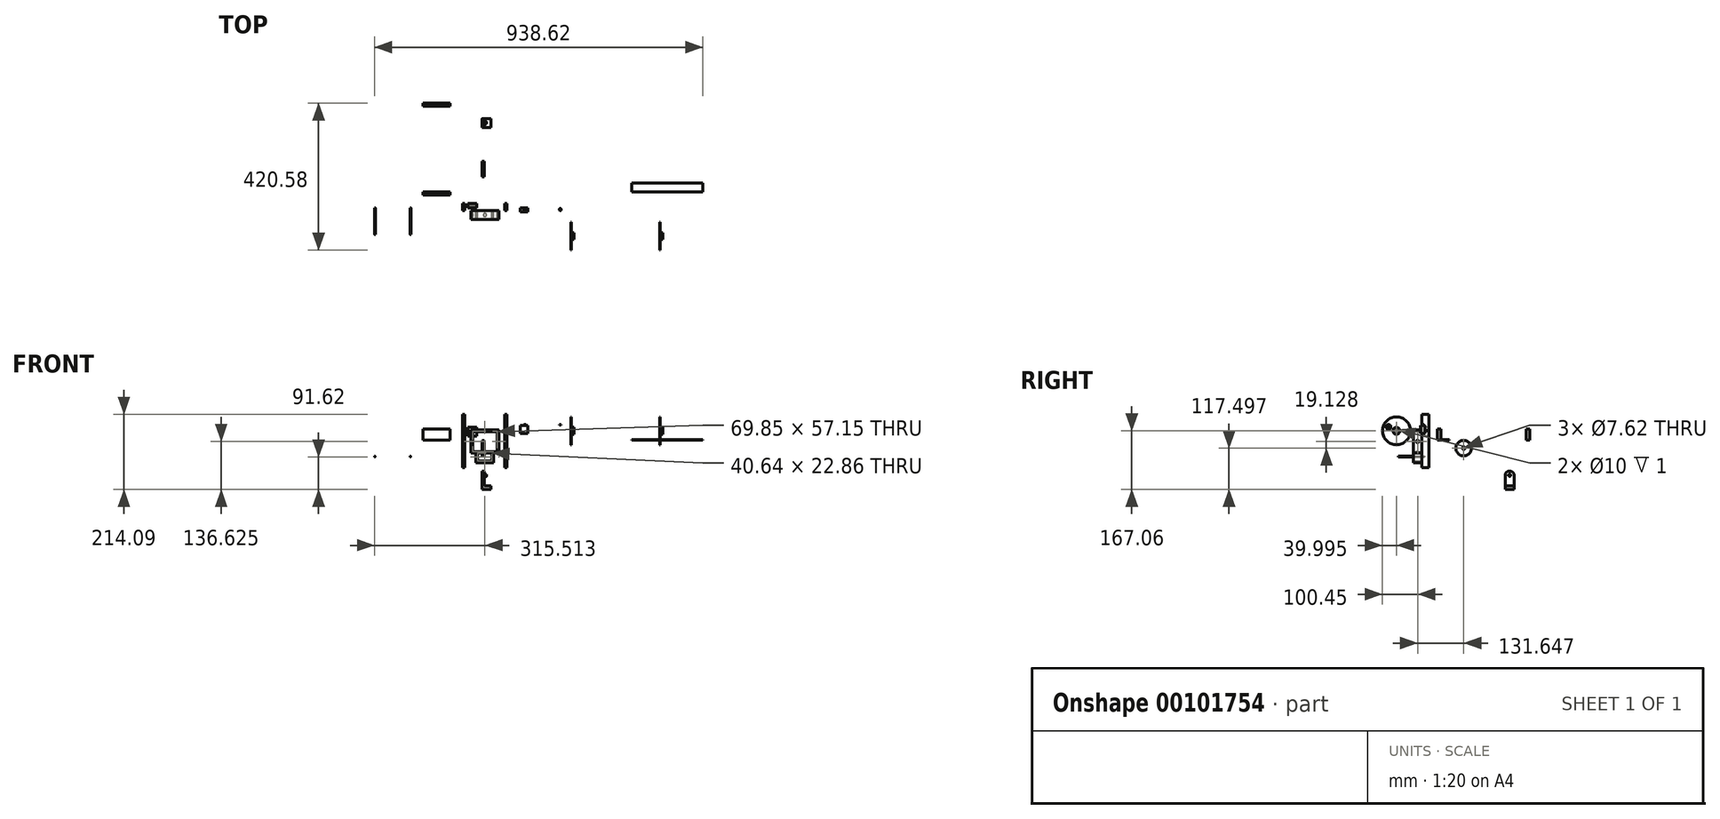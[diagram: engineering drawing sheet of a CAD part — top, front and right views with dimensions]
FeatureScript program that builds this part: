
annotation { "Feature Type Name" : "Feature", "Feature Type Description" : "" }
export const myFeature = defineFeature(function(context is Context, id is Id, definition is map)
    precondition{}
    {
        {
            var Q0;
            Q0=qCreatedBy(makeId("Front.planeOp"),FACE);
            var sketch = newSketch(context, id + "F0", { "sketchPlane" : qUnion([Q0])});
            skLineSegment(sketch, "E0.bottom", {"start": v(-56.2, 74.1) * mm, "end": v(70.8, 74.1) * mm});
            skLineSegment(sketch, "E0.top", {"start": v(-56.2, -78.3) * mm, "end": v(70.8, -78.3) * mm});
            skLineSegment(sketch, "E0.left", {"start": v(-56.2, 74.1) * mm, "end": v(-56.2, -78.3) * mm});
            skLineSegment(sketch, "E0.right", {"start": v(70.8, 74.1) * mm, "end": v(70.8, -78.3) * mm});
            skLineSegment(sketch, "E1", {"start": v(64.45, 74.1) * mm, "end": v(64.45, -78.3) * mm});
            skLineSegment(sketch, "E2", {"start": v(-49.85, 74.1) * mm, "end": v(-49.85, -78.3) * mm});
            skLineSegment(sketch, "E3", {"start": v(70.8, 74.1) * mm, "end": v(64.45, 74.1) * mm});
            skLineSegment(sketch, "E4", {"start": v(70.8, -78.3) * mm, "end": v(64.45, -78.3) * mm});
            skLineSegment(sketch, "E5", {"start": v(-49.85, 74.1) * mm, "end": v(-56.2, 74.1) * mm});
            skLineSegment(sketch, "E6", {"start": v(-49.85, -78.3) * mm, "end": v(-56.2, -78.3) * mm});
            skLineSegment(sketch, "E7", {"start": v(70.8, 10.6) * mm, "end": v(70.8, -11.63) * mm});
            skLineSegment(sketch, "E8", {"start": v(-49.85, 10.6) * mm, "end": v(-49.85, -11.63) * mm});
            skLineSegment(sketch, "E9", {"start": v(70.8, 10.6) * mm, "end": v(70.8, 74.1) * mm});
            skLineSegment(sketch, "E10", {"start": v(-49.85, 10.6) * mm, "end": v(-49.85, 74.1) * mm});
            skLineSegment(sketch, "E11", {"start": v(-49.85, 10.6) * mm, "end": v(-56.2, 10.6) * mm});
            skLineSegment(sketch, "E12", {"start": v(-49.85, -11.63) * mm, "end": v(-56.2, -11.63) * mm});
            skLineSegment(sketch, "E13", {"start": v(70.8, 10.6) * mm, "end": v(64.45, 10.6) * mm});
            skLineSegment(sketch, "E14", {"start": v(70.8, -11.63) * mm, "end": v(64.45, -11.63) * mm});
            skLineSegment(sketch, "E15", {"start": v(64.45, 10.6) * mm, "end": v(64.45, -11.63) * mm});
            skLineSegment(sketch, "E16", {"start": v(-56.2, 10.6) * mm, "end": v(-56.2, -11.63) * mm});
            skSolve(sketch);
        }
        {
            var Q0;
            Q0=makeQuery(id+"F0.imprint","IMPRINT",FACE,{"disambiguationData":[TD([[makeQuery(id+"F0.imprint","IMPRINT",EDGE,{"derivedFrom":sQuery(id+"F0.wireOp",EDGE,"E0.left")}),1.0]])]});
            var Q1;
            Q1=makeQuery(id+"F0.imprint","IMPRINT",FACE,{"disambiguationData":[TD([[makeQuery(id+"F0.imprint","IMPRINT",EDGE,{"derivedFrom":sQuery(id+"F0.wireOp",EDGE,"E0.right")}),-1.0]])]});
            var Q2;
            {var subQ0=sQuery(id+"F0.wireOp",EDGE,"E3");Q2=makeQuery(id+"F0.imprint","IMPRINT",FACE,{"disambiguationData":[TD([[makeQuery(id+"F0.imprint","IMPRINT",EDGE,{"derivedFrom":subQ0}),1.0]])]});}
            var Q3;
            {var subQ3=sQuery(id+"F0.wireOp",EDGE,"E0.bottom");Q3=makeQuery(id+"F0.imprint","IMPRINT",FACE,{"disambiguationData":[TD([[makeQuery(id+"F0.imprint","IMPRINT",EDGE,{"derivedFrom":subQ3}),-1.0]])]});}
            var Q4;
            Q4=makeQuery(id+"F0.imprint","IMPRINT",FACE,{"disambiguationData":[TD([[makeQuery(id+"F0.imprint","IMPRINT",EDGE,{"derivedFrom":sQuery(id+"F0.wireOp",EDGE,"E8")}),-1.0]])]});
            var Q5;
            Q5=makeQuery(id+"F0.imprint","IMPRINT",FACE,{"disambiguationData":[TD([[makeQuery(id+"F0.imprint","IMPRINT",EDGE,{"derivedFrom":sQuery(id+"F0.wireOp",EDGE,"E7")}),-1.0]])]});
            extrude(context, id + "F1", {"entities" : qUnion([Q0, Q1, Q2, Q3, Q4, Q5]), "depth" : 7.62 * mm});
        }
        {
            var Q0;
            Q0=qCreatedBy(makeId("Front.planeOp"),FACE);
            var sketch = newSketch(context, id + "F2", { "sketchPlane" : qUnion([Q0])});
            skLineSegment(sketch, "E17.bottom", {"start": v(108.57, 41.83) * mm, "end": v(130.8, 41.83) * mm});
            skLineSegment(sketch, "E17.top", {"start": v(108.57, 19.6) * mm, "end": v(130.8, 19.6) * mm});
            skLineSegment(sketch, "E17.left", {"start": v(108.57, 41.83) * mm, "end": v(108.57, 19.6) * mm});
            skLineSegment(sketch, "E17.right", {"start": v(130.8, 41.83) * mm, "end": v(130.8, 19.6) * mm});
            skSolve(sketch);
        }
        {
            var Q0;
            Q0=makeQuery(id+"F2.imprint","IMPRINT",FACE,{"disambiguationData":[TD([[makeQuery(id+"F2.imprint","IMPRINT",EDGE,{"derivedFrom":sQuery(id+"F2.wireOp",EDGE,"E17.bottom")}),-1.0]])]});
            extrude(context, id + "F3", {"entities" : qUnion([Q0]), "depth" : 11.94 * mm});
        }
        {
            var Q0;
            Q0=makeQuery(id+"F3.opExtrude","SWEPT_BODY",BODY,{"disambiguationData":[OSD([sQuery(id+"F2.wireOp",EDGE,"E17.bottom"),sQuery(id+"F2.wireOp",EDGE,"E17.top"),sQuery(id+"F2.wireOp",EDGE,"E17.left"),sQuery(id+"F2.wireOp",EDGE,"E17.right")])]});
            transform(context, id + "F4", {"entities" : qUnion([Q0]), "transformType" : TransformType.TRANSLATION_3D, "dx" : 76.2 * mm, "dy" : 0 * mm, "dz" : 0 * mm, "makeCopy" : true});
        }
        {
            var Q0;
            Q0=makeQuery(id+"F1.opExtrude","CAP_FACE",FACE,{"disambiguationData":[OSD([sQuery(id+"F0.wireOp",EDGE,"E0.bottom"),sQuery(id+"F0.wireOp",EDGE,"E0.top"),sQuery(id+"F0.wireOp",EDGE,"E0.left"),sQuery(id+"F0.wireOp",EDGE,"E0.right")])],"isStart":false});
            var sketch = newSketch(context, id + "F5", { "sketchPlane" : qUnion([Q0])});
            skLineSegment(sketch, "E18.bottom", {"start": v(-27, 25.2) * mm, "end": v(42.85, 25.2) * mm});
            skLineSegment(sketch, "E18.top", {"start": v(-27, -31.95) * mm, "end": v(42.85, -31.95) * mm});
            skLineSegment(sketch, "E18.left", {"start": v(-27, 25.2) * mm, "end": v(-27, -31.95) * mm});
            skLineSegment(sketch, "E18.right", {"start": v(42.85, 25.2) * mm, "end": v(42.85, -31.95) * mm});
            skLineSegment(sketch, "E19.bottom", {"start": v(-32, 30.2) * mm, "end": v(47.85, 30.2) * mm});
            skLineSegment(sketch, "E19.left", {"start": v(-32, 30.2) * mm, "end": v(-32, -36.95) * mm});
            skLineSegment(sketch, "E19.right", {"start": v(47.85, 30.2) * mm, "end": v(47.85, -36.95) * mm});
            skLineSegment(sketch, "E20", {"start": v(-12.4, -36.95) * mm, "end": v(28.24, -36.95) * mm});
            skLineSegment(sketch, "E21", {"start": v(-32, -36.95) * mm, "end": v(-17.4, -36.95) * mm});
            skLineSegment(sketch, "E22", {"start": v(33.24, -36.95) * mm, "end": v(47.85, -36.95) * mm});
            skLineSegment(sketch, "E23", {"start": v(28.24, -36.95) * mm, "end": v(28.24, -59.81) * mm});
            skLineSegment(sketch, "E24", {"start": v(-12.4, -36.95) * mm, "end": v(-12.4, -59.81) * mm});
            skLineSegment(sketch, "E25", {"start": v(-12.4, -59.81) * mm, "end": v(28.24, -59.81) * mm});
            skLineSegment(sketch, "E26", {"start": v(-17.4, -36.95) * mm, "end": v(-17.4, -64.81) * mm});
            skLineSegment(sketch, "E27", {"start": v(-17.4, -64.81) * mm, "end": v(33.24, -64.81) * mm});
            skLineSegment(sketch, "E28", {"start": v(33.24, -36.95) * mm, "end": v(33.24, -64.81) * mm});
            skSolve(sketch);
        }
        {
            var Q0;
            Q0=qCreatedBy(makeId("Right.planeOp"),FACE);
            var sketch = newSketch(context, id + "F6", { "sketchPlane" : qUnion([Q0])});
            skCircle(sketch, "E29", {"center": v(-80.77, 27.06) * mm, "radius": 40 * mm});
            skCircle(sketch, "E30", {"center": v(-80.77, 27.06) * mm, "radius": 5 * mm});
            skSolve(sketch);
        }
        {
            var Q0;
            Q0=makeQuery(id+"F6.imprint","IMPRINT",FACE,{"disambiguationData":[TD([[makeQuery(id+"F6.imprint","IMPRINT",EDGE,{"derivedFrom":sQuery(id+"F6.wireOp",EDGE,"E29")}),1.0]])]});
            extrude(context, id + "F7", {"entities" : qUnion([Q0]), "depth" : 1 * mm});
        }
        {
            var Q0;
            Q0=makeQuery(id+"F3.opExtrude","SWEPT_FACE",FACE,{"disambiguationData":[OSD([sQuery(id+"F2.wireOp",EDGE,"E17.bottom")])]});
            var sketch = newSketch(context, id + "F8", { "sketchPlane" : qUnion([Q0])});
            skCircle(sketch, "E31", {"center": v(121.91, -5) * mm, "radius": 3 * mm});
            skPoint(sketch, "E32.endSnap0", {"position": v(108.57, -5.97) * mm});
            skCircle(sketch, "E33", {"center": v(121.91, -5) * mm, "radius": 1 * mm});
            skSolve(sketch);
        }
        {
            var Q0;
            Q0=makeQuery(id+"F8.imprint","IMPRINT",FACE,{"disambiguationData":[TD([[makeQuery(id+"F8.imprint","IMPRINT",EDGE,{"derivedFrom":sQuery(id+"F8.wireOp",EDGE,"E33")}),1.0]])]});
            extrude(context, id + "F9", {"entities" : qUnion([Q0]), "operationType" : NewBodyOperationType.ADD, "depth" : 1.5 * mm});
        }
        {
            var Q0;
            Q0=makeQuery(id+"F8.imprint","IMPRINT",FACE,{"disambiguationData":[TD([[makeQuery(id+"F8.imprint","IMPRINT",EDGE,{"derivedFrom":sQuery(id+"F8.wireOp",EDGE,"E31")}),1.0]])]});
            extrude(context, id + "F10", {"entities" : qUnion([Q0]), "depth" : 1.5 * mm});
        }
        {
            var Q0;
            Q0=makeQuery(id+"F10.opExtrude","CAP_FACE",FACE,{"disambiguationData":[OSD([sQuery(id+"F8.wireOp",EDGE,"E31"),sQuery(id+"F8.wireOp",EDGE,"E33")])],"isStart":false});
            var Q1;
            Q1=makeQuery(id+"F9.opExtrude","CAP_FACE",FACE,{"disambiguationData":[OSD([sQuery(id+"F8.wireOp",EDGE,"E33")])],"isStart":false});
            extrude(context, id + "F11", {"entities" : qUnion([Q0, Q1]), "depth" : 2 * mm});
        }
        {
            var Q0;
            Q0=makeQuery(id+"F10.opExtrude","SWEPT_BODY",BODY,{"disambiguationData":[OSD([sQuery(id+"F8.wireOp",EDGE,"E31"),sQuery(id+"F8.wireOp",EDGE,"E33")])]});
            deleteBodies(context, id + "F12", {"entities" : qUnion([Q0])});
        }
        {
            var Q0;
            Q0=makeQuery(id+"F4.opPattern","COPY",BODY,{"derivedFrom":makeQuery(id+"F3.opExtrude","SWEPT_BODY",BODY,{"disambiguationData":[OSD([sQuery(id+"F2.wireOp",EDGE,"E17.bottom"),sQuery(id+"F2.wireOp",EDGE,"E17.top"),sQuery(id+"F2.wireOp",EDGE,"E17.left"),sQuery(id+"F2.wireOp",EDGE,"E17.right")])]}),"instanceName":"1"});
            deleteBodies(context, id + "F13", {"entities" : qUnion([Q0])});
        }
        {
            var Q0;
            Q0=makeQuery(id+"F11.opExtrude","SWEPT_BODY",BODY,{"disambiguationData":[OSD([sQuery(id+"F8.wireOp",EDGE,"E31"),sQuery(id+"F8.wireOp",EDGE,"E33")])]});
            transform(context, id + "F14", {"entities" : qUnion([Q0]), "transformType" : TransformType.TRANSLATION_3D, "dx" : 101.6 * mm, "dy" : 0 * mm, "dz" : 0 * mm, "makeCopy" : true});
        }
        {
            var Q0;
            Q0=makeQuery(id+"F7.opExtrude","SWEPT_BODY",BODY,{"disambiguationData":[OSD([sQuery(id+"F6.wireOp",EDGE,"E29"),sQuery(id+"F6.wireOp",EDGE,"E30")])]});
            transform(context, id + "F15", {"entities" : qUnion([Q0]), "transformType" : TransformType.TRANSLATION_3D, "dx" : 254 * mm, "dy" : 0 * mm, "dz" : 0 * mm, "makeCopy" : false});
        }
        {
            var Q0;
            Q0=makeQuery(id+"F5.imprint","IMPRINT",FACE,{"disambiguationData":[TD([[makeQuery(id+"F5.imprint","IMPRINT",EDGE,{"derivedFrom":sQuery(id+"F5.wireOp",EDGE,"E18.bottom")}),1.0]])]});
            extrude(context, id + "F16", {"entities" : qUnion([Q0]), "operationType" : NewBodyOperationType.ADD, "depth" : 25.4 * mm});
        }
        {
            var Q0;
            Q0=qCreatedBy(makeId("Front.planeOp"),FACE);
            var sketch = newSketch(context, id + "F17", { "sketchPlane" : qUnion([Q0])});
            skCircle(sketch, "E34", {"center": v(-306.58, -46.54) * mm, "radius": 1 * mm});
            skSolve(sketch);
        }
        {
            var Q0;
            Q0 = qSketchRegion(id + "F17", true);
            extrude(context, id + "F18", {"entities" : qUnion([Q0]), "depth" : 76.2 * mm});
        }
        {
            var Q0;
            Q0=makeQuery(id+"F7.opExtrude","CAP_FACE",FACE,{"disambiguationData":[OSD([sQuery(id+"F6.wireOp",EDGE,"E29"),sQuery(id+"F6.wireOp",EDGE,"E30")])],"isStart":false});
            var sketch = newSketch(context, id + "F19", { "sketchPlane" : qUnion([Q0])});
            skCircle(sketch, "E35", {"center": v(-80.77, 27.06) * mm, "radius": 10 * mm});
            skSolve(sketch);
        }
        {
            var Q0;
            Q0=makeQuery(id+"F19.imprint","IMPRINT",FACE,{"disambiguationData":[TD([[makeQuery(id+"F19.imprint","IMPRINT",EDGE,{"derivedFrom":sQuery(id+"F19.wireOp",EDGE,"E35")}),1.0]])]});
            var Q1;
            Q1=makeQuery(id+"F19.imprint","IMPRINT",FACE,{"disambiguationData":[TD([[makeQuery(id+"F19.imprint","IMPRINT",EDGE,{"derivedFrom":makeQuery(id+"F7.opExtrude","CAP_EDGE",EDGE,{"disambiguationData":[OSD([sQuery(id+"F6.wireOp",EDGE,"E30")])],"isStart":false})}),1.0]])]});
            extrude(context, id + "F20", {"entities" : qUnion([Q0, Q1]), "operationType" : NewBodyOperationType.ADD, "depth" : 7.62 * mm});
        }
        {
            var Q0;
            Q0=makeQuery(id+"F7.opExtrude","SWEPT_BODY",BODY,{"disambiguationData":[OSD([sQuery(id+"F6.wireOp",EDGE,"E29"),sQuery(id+"F6.wireOp",EDGE,"E30")])]});
            transform(context, id + "F21", {"entities" : qUnion([Q0]), "transformType" : TransformType.TRANSLATION_3D, "dx" : 254 * mm, "dy" : 0 * mm, "dz" : 0 * mm, "makeCopy" : true});
        }
        {
            var Q0;
            Q0=makeQuery(id+"F0.imprint","IMPRINT",FACE,{"disambiguationData":[TD([[makeQuery(id+"F0.imprint","IMPRINT",EDGE,{"derivedFrom":sQuery(id+"F0.wireOp",EDGE,"E0.right")}),-1.0]])]});
            var Q1;
            Q1=makeQuery(id+"F0.imprint","IMPRINT",FACE,{"disambiguationData":[TD([[makeQuery(id+"F0.imprint","IMPRINT",EDGE,{"derivedFrom":sQuery(id+"F0.wireOp",EDGE,"E0.left")}),1.0]])]});
            var Q2;
            {var subQ0=sQuery(id+"F0.wireOp",EDGE,"E3");Q2=makeQuery(id+"F0.imprint","IMPRINT",FACE,{"disambiguationData":[TD([[makeQuery(id+"F0.imprint","IMPRINT",EDGE,{"derivedFrom":subQ0}),1.0]])]});}
            extrude(context, id + "F22", {"entities" : qUnion([Q0, Q1, Q2]), "operationType" : NewBodyOperationType.ADD, "oppositeDirection" : true, "depth" : 11.94 * mm});
        }
        {
            var Q0;
            {var subQ0=sQuery(id+"F0.wireOp",EDGE,"E0.left");var subQ1=sQuery(id+"F0.wireOp",EDGE,"E16");Q0=makeQuery(id+"F22.boolean.opBoolean","MERGE",FACE,{"derivedFrom":[makeQuery(id+"F1.opExtrude","SWEPT_FACE",FACE,{"disambiguationData":[OSD([subQ0,subQ1])]}),makeQuery(id+"F22.opExtrude","SWEPT_FACE",FACE,{"disambiguationData":[OSD([subQ0]),TDD([makeQuery(id+"F0.imprint","IMPRINT",EDGE,{"disambiguationData":[TD([[makeQuery(id+"F0.imprint","INTERSECT",VERTEX,{"derivedFrom":[subQ0,sQuery(id+"F0.wireOp",EDGE,"E5")]}),-1.0]])],"derivedFrom":subQ0})])]}),makeQuery(id+"F22.opExtrude","SWEPT_FACE",FACE,{"disambiguationData":[OSD([subQ0]),TDD([makeQuery(id+"F0.imprint","IMPRINT",EDGE,{"disambiguationData":[TD([[makeQuery(id+"F0.imprint","INTERSECT",VERTEX,{"derivedFrom":[subQ0,sQuery(id+"F0.wireOp",EDGE,"E6")]}),1.0]])],"derivedFrom":subQ0})])]})]});}
            var sketch = newSketch(context, id + "F23", { "sketchPlane" : qUnion([Q0])});
            skLineSegment(sketch, "E36", {"start": v(-11.94, 74.1) * mm, "end": v(-11.94, 10.6) * mm});
            skLineSegment(sketch, "E37", {"start": v(-11.94, 10.6) * mm, "end": v(-5.97, 10.6) * mm});
            skLineSegment(sketch, "E38", {"start": v(-5.97, 10.6) * mm, "end": v(-5.97, 27.69) * mm});
            skCircle(sketch, "E39", {"center": v(-5.97, 27.69) * mm, "radius": 1.07 * mm});
            skSolve(sketch);
        }
        {
            var Q0;
            Q0=qCreatedBy(makeId("Top.planeOp"),FACE);
            var sketch = newSketch(context, id + "F24", { "sketchPlane" : qUnion([Q0])});
            skLineSegment(sketch, "E40.bottom", {"start": v(-169.62, 45.81) * mm, "end": v(-91.83, 45.81) * mm});
            skLineSegment(sketch, "E40.top", {"start": v(-169.62, 36.29) * mm, "end": v(-91.83, 36.29) * mm});
            skLineSegment(sketch, "E40.left", {"start": v(-169.62, 45.81) * mm, "end": v(-169.62, 36.29) * mm});
            skLineSegment(sketch, "E40.right", {"start": v(-91.83, 45.81) * mm, "end": v(-91.83, 36.29) * mm});
            skSolve(sketch);
        }
        {
            var Q0;
            Q0 = qSketchRegion(id + "F24", true);
            extrude(context, id + "F25", {"entities" : qUnion([Q0]), "depth" : 31.75 * mm});
        }
        {
            var Q0;
            Q0=makeQuery(id+"F25.opExtrude","SWEPT_BODY",BODY,{"disambiguationData":[OSD([sQuery(id+"F24.wireOp",EDGE,"E40.bottom"),sQuery(id+"F24.wireOp",EDGE,"E40.top"),sQuery(id+"F24.wireOp",EDGE,"E40.left"),sQuery(id+"F24.wireOp",EDGE,"E40.right")])]});
            transform(context, id + "F26", {"entities" : qUnion([Q0]), "transformType" : TransformType.TRANSLATION_3D, "dx" : 0 * mm, "dy" : 254 * mm, "dz" : 0 * mm, "makeCopy" : true});
        }
        {
            var Q0;
            Q0=qCreatedBy(makeId("Top.planeOp"),FACE);
            var sketch = newSketch(context, id + "F27", { "sketchPlane" : qUnion([Q0])});
            skLineSegment(sketch, "E41.bottom", {"start": v(-80.17, 70.92) * mm, "end": v(123.03, 70.92) * mm});
            skLineSegment(sketch, "E41.top", {"start": v(-80.17, 45.52) * mm, "end": v(123.03, 45.52) * mm});
            skLineSegment(sketch, "E41.left", {"start": v(-80.17, 70.92) * mm, "end": v(-80.17, 45.52) * mm});
            skLineSegment(sketch, "E41.right", {"start": v(123.03, 70.92) * mm, "end": v(123.03, 45.52) * mm});
            skSolve(sketch);
        }
        {
            var Q0;
            Q0=makeQuery(id+"F27.imprint","IMPRINT",FACE,{"disambiguationData":[TD([[makeQuery(id+"F27.imprint","IMPRINT",EDGE,{"derivedFrom":sQuery(id+"F27.wireOp",EDGE,"E41.bottom")}),-1.0]])]});
            extrude(context, id + "F28", {"entities" : qUnion([Q0]), "depth" : 1.27 * mm});
        }
        {
            var Q0;
            Q0=qCreatedBy(makeId("Right.planeOp"),FACE);
            var sketch = newSketch(context, id + "F29", { "sketchPlane" : qUnion([Q0])});
            skLineSegment(sketch, "E42.bottom", {"start": v(230.23, -140) * mm, "end": v(255.63, -140) * mm});
            skLineSegment(sketch, "E42.top", {"start": v(241.66, -88.57) * mm, "end": v(244.2, -88.57) * mm});
            skLineSegment(sketch, "E42.left", {"start": v(230.23, -140) * mm, "end": v(230.23, -100) * mm});
            skLineSegment(sketch, "E42.right", {"start": v(255.63, -140) * mm, "end": v(255.63, -100) * mm});
            skArc(sketch, "E43.filletArc", {"start": v(241.66, -88.57) * mm, "mid": v(233.58, -91.92) * mm, "end": v(230.23, -100) * mm});
            skArc(sketch, "E44.filletArc", {"start": v(255.63, -100) * mm, "mid": v(252.28, -91.92) * mm, "end": v(244.2, -88.57) * mm});
            skLineSegment(sketch, "E45", {"start": v(230.23, -122.33) * mm, "end": v(242.93, -122.33) * mm});
            skCircle(sketch, "E46", {"center": v(242.93, -100) * mm, "radius": 3.18 * mm});
            skLineSegment(sketch, "E47", {"start": v(230.23, -130) * mm, "end": v(242.93, -130) * mm});
            skLineSegment(sketch, "E48", {"start": v(242.93, -130) * mm, "end": v(255.63, -130) * mm});
            skLineSegment(sketch, "E49", {"start": v(242.93, -130) * mm, "end": v(242.93, -140) * mm});
            skSolve(sketch);
        }
        {
            var Q0;
            {var subQ4=sQuery(id+"F29.wireOp",EDGE,"E47");Q0=makeQuery(id+"F29.imprint","IMPRINT",FACE,{"disambiguationData":[TD([[makeQuery(id+"F29.imprint","IMPRINT",EDGE,{"derivedFrom":subQ4}),-1.0]])]});}
            var Q1;
            {var subQ4=sQuery(id+"F29.wireOp",EDGE,"E48");Q1=makeQuery(id+"F29.imprint","IMPRINT",FACE,{"disambiguationData":[TD([[makeQuery(id+"F29.imprint","IMPRINT",EDGE,{"derivedFrom":subQ4}),-1.0]])]});}
            var Q2;
            {var subQ0=sQuery(id+"F29.wireOp",EDGE,"E46");var subQ1=sQuery(id+"F29.wireOp",EDGE,"DbK4IInD-QZOi-9ule-fGbz-oK8GEeGPwDpE");var subQ2=makeQuery(id+"F29.imprint","INTERSECT",VERTEX,{"disambiguationData":[OD(0.0)],"derivedFrom":[subQ1,subQ0]});Q2=makeQuery(id+"F29.imprint","IMPRINT",FACE,{"disambiguationData":[TD([[makeQuery(id+"F29.imprint","IMPRINT",EDGE,{"disambiguationData":[TD([[subQ2,-1.0]])],"derivedFrom":subQ1}),-1.0]])]});}
            var Q3;
            {var subQ0=sQuery(id+"F29.wireOp",EDGE,"E46");var subQ1=sQuery(id+"F29.wireOp",EDGE,"DbK4IInD-QZOi-9ule-fGbz-oK8GEeGPwDpE");var subQ2=makeQuery(id+"F29.imprint","INTERSECT",VERTEX,{"disambiguationData":[OD(0.0)],"derivedFrom":[subQ1,subQ0]});Q3=makeQuery(id+"F29.imprint","IMPRINT",FACE,{"disambiguationData":[TD([[makeQuery(id+"F29.imprint","IMPRINT",EDGE,{"disambiguationData":[TD([[subQ2,-1.0]])],"derivedFrom":subQ1}),1.0]])]});}
            var Q4;
            Q4=makeQuery(id+"F29.imprint","IMPRINT",FACE,{"disambiguationData":[TD([[makeQuery(id+"F29.imprint","IMPRINT",EDGE,{"derivedFrom":sQuery(id+"F29.wireOp",EDGE,"E46")}),1.0]])]});
            extrude(context, id + "F30", {"entities" : qUnion([Q0, Q1, Q2, Q3, Q4]), "depth" : 12.7 * mm});
        }
        {
            var Q0;
            {var subQ9=sQuery(id+"F29.wireOp",EDGE,"E47");Q0=makeQuery(id+"F29.imprint","IMPRINT",FACE,{"disambiguationData":[TD([[makeQuery(id+"F29.imprint","IMPRINT",EDGE,{"derivedFrom":subQ9}),1.0]])]});}
            var Q1;
            Q1=makeQuery(id+"F29.imprint","IMPRINT",FACE,{"disambiguationData":[TD([[makeQuery(id+"F29.imprint","IMPRINT",EDGE,{"derivedFrom":sQuery(id+"F29.wireOp",EDGE,"E42.top")}),-1.0]])]});
            extrude(context, id + "F31", {"entities" : qUnion([Q0, Q1]), "depth" : 6.35 * mm});
        }
        {
            var Q0;
            Q0=makeQuery(id+"F30.opExtrude","SWEPT_BODY",BODY,{"disambiguationData":[OSD([sQuery(id+"F29.wireOp",EDGE,"E42.bottom"),sQuery(id+"F29.wireOp",EDGE,"E42.left"),sQuery(id+"F29.wireOp",EDGE,"E42.right"),sQuery(id+"F29.wireOp",EDGE,"E47"),sQuery(id+"F29.wireOp",EDGE,"E48")])]});
            var Q1;
            Q1=makeQuery(id+"F30.opExtrude","CAP_FACE",FACE,{"disambiguationData":[OSD([sQuery(id+"F29.wireOp",EDGE,"E42.bottom"),sQuery(id+"F29.wireOp",EDGE,"E42.left"),sQuery(id+"F29.wireOp",EDGE,"E42.right"),sQuery(id+"F29.wireOp",EDGE,"E47"),sQuery(id+"F29.wireOp",EDGE,"E48")])],"isStart":false});
            mirror(context, id + "F32", {"operationType" : NewBodyOperationType.ADD, "entities" : qUnion([Q0]), "mirrorPlane" : qUnion([Q1])});
        }
        {
            var Q0;
            Q0=qCreatedBy(makeId("Right.planeOp"),FACE);
            var sketch = newSketch(context, id + "F33", { "sketchPlane" : qUnion([Q0])});
            skCircle(sketch, "E50", {"center": v(111.33, -22.5) * mm, "radius": 22.23 * mm});
            skCircle(sketch, "E51", {"center": v(111.33, -22.5) * mm, "radius": 3.8 * mm});
            skSolve(sketch);
        }
        {
            var Q0;
            Q0=makeQuery(id+"F33.imprint","IMPRINT",FACE,{"disambiguationData":[TD([[makeQuery(id+"F33.imprint","IMPRINT",EDGE,{"derivedFrom":sQuery(id+"F33.wireOp",EDGE,"E50")}),1.0]])]});
            extrude(context, id + "F34", {"entities" : qUnion([Q0]), "depth" : 6.35 * mm});
        }
        {
            var Q0;
            Q0=makeQuery(id+"F16.opExtrude","SWEPT_FACE",FACE,{"disambiguationData":[OSD([sQuery(id+"F5.wireOp",EDGE,"E20")])]});
            var sketch = newSketch(context, id + "F35", { "sketchPlane" : qUnion([Q0])});
            skLineSegment(sketch, "E52", {"start": v(-12.4, 33.02) * mm, "end": v(7.92, 33.02) * mm});
            skLineSegment(sketch, "E53", {"start": v(-12.4, 33.02) * mm, "end": v(-12.4, 20.32) * mm});
            skCircle(sketch, "E54", {"center": v(7.93, 20.32) * mm, "radius": 4.45 * mm});
            skSolve(sketch);
        }
        {
            var Q0;
            Q0=makeQuery(id+"F35.imprint","IMPRINT",FACE,{"disambiguationData":[TD([[makeQuery(id+"F35.imprint","IMPRINT",EDGE,{"derivedFrom":sQuery(id+"F35.wireOp",EDGE,"E54")}),1.0]])]});
            extrude(context, id + "F36", {"entities" : qUnion([Q0]), "operationType" : NewBodyOperationType.REMOVE, "oppositeDirection" : true, "depth" : 25.4 * mm});
        }
        {
            var Q0;
            Q0=makeQuery(id+"F16.opExtrude","SWEPT_FACE",FACE,{"disambiguationData":[OSD([sQuery(id+"F5.wireOp",EDGE,"E19.right")])]});
            var sketch = newSketch(context, id + "F37", { "sketchPlane" : qUnion([Q0])});
            skLineSegment(sketch, "E55", {"start": v(-33.02, 30.2) * mm, "end": v(-20.32, 30.2) * mm});
            skLineSegment(sketch, "E56", {"start": v(-33.02, 30.2) * mm, "end": v(-33.02, -3.38) * mm});
            skLineSegment(sketch, "E57.left", {"start": v(-33.02, -3.38) * mm, "end": v(-33.02, 30.2) * mm});
            skCircle(sketch, "E58", {"center": v(-20.32, -3.38) * mm, "radius": 3.81 * mm});
            skSolve(sketch);
        }
        {
            var Q0;
            Q0=makeQuery(id+"F37.imprint","IMPRINT",FACE,{"disambiguationData":[TD([[makeQuery(id+"F37.imprint","IMPRINT",EDGE,{"derivedFrom":sQuery(id+"F37.wireOp",EDGE,"E58")}),1.0]])]});
            extrude(context, id + "F38", {"entities" : qUnion([Q0]), "operationType" : NewBodyOperationType.REMOVE, "oppositeDirection" : true, "depth" : 88.9 * mm});
        }
        {
            var Q0;
            {var subQ0=sQuery(id+"F0.wireOp",EDGE,"E6");var subQ1=sQuery(id+"F0.wireOp",EDGE,"E4");var subQ2=sQuery(id+"F0.wireOp",EDGE,"E0.top");var subQ3=sQuery(id+"F0.wireOp",EDGE,"E5");var subQ4=sQuery(id+"F0.wireOp",EDGE,"E3");var subQ5=sQuery(id+"F0.wireOp",EDGE,"E0.bottom");var subQ6=sQuery(id+"F0.wireOp",EDGE,"E16");var subQ7=sQuery(id+"F0.wireOp",EDGE,"E0.left");var subQ8=sQuery(id+"F0.wireOp",EDGE,"E9");var subQ9=sQuery(id+"F0.wireOp",EDGE,"E7");var subQ10=sQuery(id+"F0.wireOp",EDGE,"E0.right");Q0=makeQuery(id+"F16.boolean.opBoolean","SPLIT",FACE,{"disambiguationData":[TD([makeQuery(id+"F16.opExtrude","SWEPT_FACE",FACE,{"disambiguationData":[OSD([sQuery(id+"F5.wireOp",EDGE,"E19.bottom")])]})])],"derivedFrom":makeQuery(id+"F1.opExtrude","CAP_FACE",FACE,{"disambiguationData":[OSD([subQ5,subQ2,subQ7,subQ10,subQ4,subQ1,subQ3,subQ0,subQ9,subQ8,subQ6])],"isStart":false})});}
            var sketch = newSketch(context, id + "F39", { "sketchPlane" : qUnion([Q0])});
            skLineSegment(sketch, "E59", {"start": v(47.85, 30.2) * mm, "end": v(47.85, -36.95) * mm});
            skLineSegment(sketch, "E60", {"start": v(47.85, 30.2) * mm, "end": v(60.55, 30.2) * mm});
            skLineSegment(sketch, "E61.bottom", {"start": v(60.55, 30.2) * mm, "end": v(47.85, 30.2) * mm});
            skLineSegment(sketch, "E61.top", {"start": v(60.55, -36.95) * mm, "end": v(47.85, -36.95) * mm});
            skLineSegment(sketch, "E61.left", {"start": v(60.55, 30.2) * mm, "end": v(60.55, -36.95) * mm});
            skLineSegment(sketch, "E62", {"start": v(47.85, 30.2) * mm, "end": v(47.85, -3.38) * mm});
            skLineSegment(sketch, "E63", {"start": v(47.85, 30.2) * mm, "end": v(54.2, 30.2) * mm});
            skLineSegment(sketch, "E64.left", {"start": v(47.85, -3.38) * mm, "end": v(47.85, 30.2) * mm});
            skCircle(sketch, "E65", {"center": v(54.2, -3.38) * mm, "radius": 3.81 * mm});
            skSolve(sketch);
        }
        {
            var Q0;
            Q0=makeQuery(id+"F39.imprint","IMPRINT",FACE,{"disambiguationData":[TD([[makeQuery(id+"F39.imprint","IMPRINT",EDGE,{"derivedFrom":sQuery(id+"F39.wireOp",EDGE,"E65")}),1.0]])]});
            extrude(context, id + "F40", {"entities" : qUnion([Q0]), "operationType" : NewBodyOperationType.REMOVE, "oppositeDirection" : true, "depth" : 25.4 * mm});
        }
        {
            var Q0;
            {var subQ0=sQuery(id+"F0.wireOp",EDGE,"E6");var subQ1=sQuery(id+"F0.wireOp",EDGE,"E4");var subQ2=sQuery(id+"F0.wireOp",EDGE,"E0.top");var subQ3=sQuery(id+"F0.wireOp",EDGE,"E5");var subQ4=sQuery(id+"F0.wireOp",EDGE,"E3");var subQ5=sQuery(id+"F0.wireOp",EDGE,"E0.bottom");var subQ6=sQuery(id+"F0.wireOp",EDGE,"E16");var subQ7=sQuery(id+"F0.wireOp",EDGE,"E0.left");var subQ8=sQuery(id+"F0.wireOp",EDGE,"E9");var subQ9=sQuery(id+"F0.wireOp",EDGE,"E7");var subQ10=sQuery(id+"F0.wireOp",EDGE,"E0.right");Q0=makeQuery(id+"F16.boolean.opBoolean","SPLIT",FACE,{"disambiguationData":[TD([makeQuery(id+"F16.opExtrude","SWEPT_FACE",FACE,{"disambiguationData":[OSD([sQuery(id+"F5.wireOp",EDGE,"E19.bottom")])]})])],"derivedFrom":makeQuery(id+"F1.opExtrude","CAP_FACE",FACE,{"disambiguationData":[OSD([subQ5,subQ2,subQ7,subQ10,subQ4,subQ1,subQ3,subQ0,subQ9,subQ8,subQ6])],"isStart":false})});}
            var sketch = newSketch(context, id + "F41", { "sketchPlane" : qUnion([Q0])});
            skLineSegment(sketch, "E66", {"start": v(-32, -36.95) * mm, "end": v(-44.7, -36.95) * mm});
            skLineSegment(sketch, "E67", {"start": v(-32, -36.95) * mm, "end": v(-32, -3.38) * mm});
            skLineSegment(sketch, "E68.bottom", {"start": v(-38.35, -36.95) * mm, "end": v(-32, -36.95) * mm});
            skCircle(sketch, "E69", {"center": v(-38.35, -3.38) * mm, "radius": 3.81 * mm});
            skSolve(sketch);
        }
        {
            var Q0;
            Q0=makeQuery(id+"F41.imprint","IMPRINT",FACE,{"disambiguationData":[TD([[makeQuery(id+"F41.imprint","IMPRINT",EDGE,{"derivedFrom":sQuery(id+"F41.wireOp",EDGE,"E69")}),1.0]])]});
            extrude(context, id + "F42", {"entities" : qUnion([Q0]), "operationType" : NewBodyOperationType.REMOVE, "oppositeDirection" : true, "depth" : 25.4 * mm});
        }
        {
            var Q0;
            Q0=makeQuery(id+"F18.opExtrude","SWEPT_BODY",BODY,{"disambiguationData":[OSD([sQuery(id+"F17.wireOp",EDGE,"E34")])]});
            transform(context, id + "F43", {"entities" : qUnion([Q0]), "transformType" : TransformType.TRANSLATION_3D, "dx" : 101.6 * mm, "dy" : 0 * mm, "dz" : 0 * mm, "makeCopy" : true});
        }
        {
            var Q0;
            Q0=makeQuery(id+"F28.opExtrude","SWEPT_BODY",BODY,{"disambiguationData":[OSD([sQuery(id+"F27.wireOp",EDGE,"E41.bottom"),sQuery(id+"F27.wireOp",EDGE,"E41.top"),sQuery(id+"F27.wireOp",EDGE,"E41.left"),sQuery(id+"F27.wireOp",EDGE,"E41.right")])]});
            transform(context, id + "F44", {"entities" : qUnion([Q0]), "transformType" : TransformType.TRANSLATION_3D, "dx" : 508 * mm, "dy" : 0 * mm, "dz" : 0 * mm, "makeCopy" : false});
        }
        {
            var Q0;
            {var subQ3=sQuery(id+"F0.wireOp",EDGE,"E0.bottom");Q0=makeQuery(id+"F0.imprint","IMPRINT",FACE,{"disambiguationData":[TD([[makeQuery(id+"F0.imprint","IMPRINT",EDGE,{"derivedFrom":subQ3}),-1.0]])]});}
            var sketch = newSketch(context, id + "F45", { "sketchPlane" : qUnion([Q0])});
            skLineSegment(sketch, "E70.bottom", {"start": v(54.9, 36.86) * mm, "end": v(29.5, 36.86) * mm});
            skLineSegment(sketch, "E70.top", {"start": v(54.9, 11.46) * mm, "end": v(29.5, 11.46) * mm});
            skLineSegment(sketch, "E71", {"start": v(54.9, 36.86) * mm, "end": v(54.9, 11.46) * mm});
            skLineSegment(sketch, "E72", {"start": v(-40.34, 11.46) * mm, "end": v(-40.34, 36.86) * mm});
            skLineSegment(sketch, "E73", {"start": v(-14.94, 11.46) * mm, "end": v(-14.94, 36.86) * mm});
            skLineSegment(sketch, "E74", {"start": v(29.5, 11.46) * mm, "end": v(29.5, 36.86) * mm});
            skLineSegment(sketch, "E75.bottom", {"start": v(29.5, 11.46) * mm, "end": v(54.9, 11.46) * mm});
            skLineSegment(sketch, "E75.top", {"start": v(29.5, 36.86) * mm, "end": v(54.9, 36.86) * mm});
            skLineSegment(sketch, "E75.right", {"start": v(54.9, 11.46) * mm, "end": v(54.9, 36.86) * mm});
            skLineSegment(sketch, "E76.left", {"start": v(29.5, 36.86) * mm, "end": v(29.5, 11.46) * mm});
            skLineSegment(sketch, "E76.right", {"start": v(-14.94, 36.86) * mm, "end": v(-14.94, 11.46) * mm});
            skLineSegment(sketch, "E77.bottom", {"start": v(-40.34, 11.46) * mm, "end": v(-14.94, 11.46) * mm});
            skLineSegment(sketch, "E77.top", {"start": v(-40.34, 36.86) * mm, "end": v(-14.94, 36.86) * mm});
            skLineSegment(sketch, "E78.left", {"start": v(-40.34, 36.86) * mm, "end": v(-40.34, 11.46) * mm});
            skLineSegment(sketch, "E79", {"start": v(-14.94, 36.86) * mm, "end": v(-40.34, 36.86) * mm});
            skSolve(sketch);
        }
        {
            var Q0;
            Q0=makeQuery(id+"F45.imprint","IMPRINT",FACE,{"disambiguationData":[TD([[makeQuery(id+"F45.imprint","IMPRINT",EDGE,{"derivedFrom":sQuery(id+"F45.wireOp",EDGE,"E77.bottom")}),1.0]])]});
            var Q1;
            Q1=makeQuery(id+"F45.imprint","IMPRINT",FACE,{"disambiguationData":[TD([[makeQuery(id+"F45.imprint","IMPRINT",EDGE,{"derivedFrom":sQuery(id+"F45.wireOp",EDGE,"E75.bottom")}),1.0]])]});
            extrude(context, id + "F46", {"entities" : qUnion([Q0, Q1]), "operationType" : NewBodyOperationType.ADD, "oppositeDirection" : true, "depth" : 12.7 * mm});
        }
        {
            var Q0;
            Q0=makeQuery(id+"F23.imprint","IMPRINT",FACE,{"disambiguationData":[TD([[makeQuery(id+"F23.imprint","IMPRINT",EDGE,{"derivedFrom":sQuery(id+"F23.wireOp",EDGE,"E39")}),1.0]])]});
            extrude(context, id + "F47", {"entities" : qUnion([Q0]), "operationType" : NewBodyOperationType.REMOVE, "oppositeDirection" : true, "depth" : 152.4 * mm});
        }
        {
            var Q0;
            Q0=makeQuery(id+"F7.opExtrude","CAP_FACE",FACE,{"disambiguationData":[OSD([sQuery(id+"F6.wireOp",EDGE,"E29"),sQuery(id+"F6.wireOp",EDGE,"E30")])],"isStart":true});
            var sketch = newSketch(context, id + "F48", { "sketchPlane" : qUnion([Q0])});
            skCircle(sketch, "E80", {"center": v(99.76, 35.99) * mm, "radius": 3.27 * mm});
            skSolve(sketch);
        }
        {
            var Q0;
            Q0=makeQuery(id+"F48.imprint","IMPRINT",FACE,{"disambiguationData":[TD([[makeQuery(id+"F48.imprint","IMPRINT",EDGE,{"derivedFrom":sQuery(id+"F48.wireOp",EDGE,"E80")}),1.0]])]});
            extrude(context, id + "F49", {"entities" : qUnion([Q0]), "operationType" : NewBodyOperationType.REMOVE, "oppositeDirection" : true, "depth" : 25400 * mm});
        }
        {
            var Q0;
            Q0=makeQuery(id+"F21.opPattern","COPY",FACE,{"derivedFrom":makeQuery(id+"F7.opExtrude","CAP_FACE",FACE,{"disambiguationData":[OSD([sQuery(id+"F6.wireOp",EDGE,"E29"),sQuery(id+"F6.wireOp",EDGE,"E30")])],"isStart":true}),"instanceName":"1"});
            var sketch = newSketch(context, id + "F50", { "sketchPlane" : qUnion([Q0])});
            skCircle(sketch, "E81", {"center": v(103.53, 38.19) * mm, "radius": 6.8 * mm});
            skSolve(sketch);
        }
        {
            var Q0;
            Q0=makeQuery(id+"F50.imprint","IMPRINT",FACE,{"disambiguationData":[TD([[makeQuery(id+"F50.imprint","IMPRINT",EDGE,{"derivedFrom":sQuery(id+"F50.wireOp",EDGE,"E81")}),1.0]])]});
            extrude(context, id + "F51", {"entities" : qUnion([Q0]), "operationType" : NewBodyOperationType.REMOVE, "oppositeDirection" : true, "depth" : 25.4 * mm});
        }
    });
